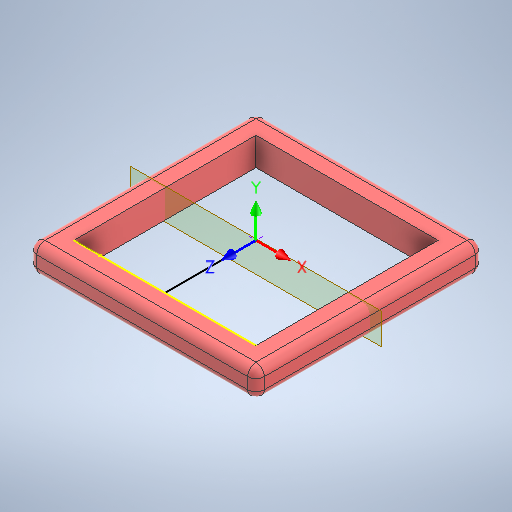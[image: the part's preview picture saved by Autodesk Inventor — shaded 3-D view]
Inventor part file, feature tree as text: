
AUTODESK INVENTOR PART (.ipt)
format: ipt  version: 2025 (Build 290162000, 162)  size: 322,048 bytes
history: native  units: in
note: dims shown in document units (in); Inventor stores cm internally (conversion verified against a paired STEP export)
features: other x9, sketch x3, extrude x2, fillet x2, shell x1, plane x1, pattern_circular x1
ambient origin geometry x8: Origin, YZ Plane, XZ Plane, XY Plane, X Axis, Y Axis, Z Axis, Center Point
bodies: Solid1 (feature_tree)
feature tree (19):
  extrude  "Extrusion1"  Depth=4.625in
  extrude  "Extrusion2"  Depth=3.75in
  fillet  "Fillet1"  Radius=3.75in
  shell  "Shell1"  Thickness=0.0in
  sketch  "Sketch4"  dims[d10=1.375in d11=0.05in d13=0.0in d14=0.0in d15=0.0in d16=0.0in d17=0.0in d18=0.0in d19=1.5748in d20=360.0deg d23=1.375in]
  other  "UCS1"
  plane  "Work Plane1"
  pattern_circular  "Circular Pattern1"  [2 undecoded]
  fillet  "Fillet3"  Radius=1.5748in
  sketch  "Sketch1"  dims[d0=37.5in d1=4.625in]
  sketch  "Sketch3"  dims[d2=3.75in d3=0.0in d6=3.75in d7=3.75in d8=0.0in d9=0.0in]
  other  "UCS1: YZ Plane"
  other  "UCS1: XZ Plane"
  other  "UCS1: XY Plane"
  other  "UCS1: X Axis"
  other  "UCS1: Y Axis"
  other  "UCS1: Z Axis"
  other  "UCS1: Center Point"
  other  "Finish1"
note: 2 required parameter values undecoded (feature->parameter linkage not recoverable at this tier; creation-order binding heuristic only, values carry confidence <= 0.55)
